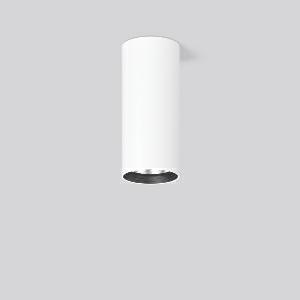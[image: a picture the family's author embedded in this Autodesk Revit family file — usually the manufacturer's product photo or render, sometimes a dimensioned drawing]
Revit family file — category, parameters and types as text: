
# Revit family: heledon_mini_a_931208_002_3_76_ec87
name_source: partatom
category: Lighting Fixtures
units: mm (PartAtom-declared; Revit-internal decimal feet)

## family parameters
Cut with Voids When Loaded = No
Host = Face
Light Source = No
Part Type = Normal
Room Calculation Point = No
Round Connector Dimension = Use Diameter
Shared = No

## types (1)
- HELEDON mini A (1 x LED Modul 935, 3700 lm, 3500)
    Apparent Load = 29 VA
    Approval mark = CE
    CIE Flux Codes = 100 100 100 100 100
    Color Rendering = 92
    Color Temperature = 3500
    Default Elevation = 1800 mm
    Description = Series: HELEDON mini
Cylindrical surface-mounted downlight. Housing: die-cast aluminium, powder-coated. Internal ceiling frame polycarbonate with bayonet mounting. Black plastic ring and recessed LED to prevent glare from the side. Optical assembly with reflector made of MIRO-Silver with 98% total light reflection for outstanding efficiency - can be changed without tools. Best colour rendering index Ra>90. Suitable for Ceiling mounting. Easy installation with a separate ceiling frame with bayonet mounting and plug connection. Driver integrated. Connected via plug-in connector. High quality converter without flickering and stroboscopic effect. The following accessories can be mounted without use of tools: interchangeable lenses, decorative glasses, honeycomb louvre, clear and frosted diffusers, white interchangeable plastic ring. 
Colour: traffic white, matt (RAL 9016)
Diameter: 87 mm
Height: 197 mm
Lamp: LED
Socket: without socket
Colour temperature: 3500K
Colour rendering index (CRI): 92
System power: 29 W
Rated luminous flux: 3700 lm
Luminous efficiency: 128 lm/W
Control gear: Converter, dimmable, DALI
Protection class: I
Type of protection: IP 20
    Height = 197 mm
    Lamp = 1 x LED Modul 935
    Lamp Light Flux = 3700 lm
    Lamp count = 1
    Length = 87 mm
    Lifetime = 50000 h
    Luminous efficacy = 128 lm/W
    Manufacturer = RZB
    ModVariant = No
    Model = 931208.002.3.76
    Mounting Place = Ceiling
    Mounting Type = Surface mounted
    Number of Poles = 1
    OnlyDefault = Yes
    Power Factor = 1
    Product Name = HELEDON mini A
    Product group = Surface mounted downlights
    ProductGroupID = 302
    Protection Class = Protection class I
    Protection Degree = IP 20
    RLX_Detail_Level = 1
    RLX_Emergency_Light_Flux = 0 lm
    RLX_Emergency_Type = 0
    RLX_Emergency_Type_DB = No
    RlxData = <blob elided: 106793 chars, md5=59582693>
    Socket = socket
    Standby Power = 0 W
    System Light Flux = 3700 lm
    System Power = 29 W
    Type Comments = Product without accessories
    Type Image = 931188.002.jpg
    URL = http://relux.com
    VarID = ---
    Voltage = 230 V
    Voltage Range = 220-240 V
    Weight = 0.00 kg
    Width = 0 mm  [stored 0 ft]

note: [stored X ft] marks values corroborated as IEEE doubles in the binary element streams (Revit-internal decimal feet)

## geometry (parser evidence)
native form markers: Blend x4, Sweep x9
no freeform markers — native parametric forms only
